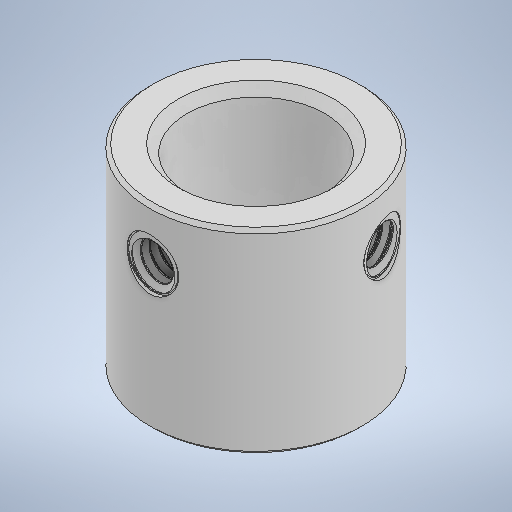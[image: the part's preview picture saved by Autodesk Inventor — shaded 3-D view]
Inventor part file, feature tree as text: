
AUTODESK INVENTOR PART (.ipt)
format: ipt  version: 2025.2 (Build 292293000, 293)  size: 747,520 bytes
history: native  units: mm
features: chamfer x2, extrude x1, plane x1, hole x1, thread x1, revolve x1, helix x1, pattern_circular x1, sketch x1
ambient origin geometry x8: Origin, YZ Plane, XZ Plane, XY Plane, X Axis, Y Axis, Z Axis, Center Point
bodies: Solid1 (feature_tree), Solid2 (feature_tree)
feature tree (10):
  extrude  "Extrusion1"  Depth=0.5005mm TaperAngle=45.0deg
  chamfer  "Chamfer1"  Distance=0.2mm Angle=45.0deg
  chamfer  "Chamfer2"  Distance=8.0mm
  plane  "Work Plane1"
  hole  "Hole1"  [1 undecoded]
  thread  "Thread1"  [1 undecoded]
  revolve  "Revolution1"  [1 undecoded]
  helix  "Coil1"  [1 undecoded]
  pattern_circular  "Circular Pattern1"  [2 undecoded]
  sketch  "Sketch4"  dims[d0=11.35mm d1=0.0mm d2=0.5mm d3=2.0mm d4=45.0deg d5=0.2mm d6=2.0mm d7=45.0deg d8=8.0mm d9=12.35mm d10=6.175mm d11=3.0mm d12=2.85mm d13=6.0mm d14=3.0mm d15=0.2mm d16=90.0deg d17=6.175mm d18=0.0mm d19=2.0mm d20=0.0mm d21=9.599311mm d22=0.080042mm d23=0.080042mm d26=0.5mm d28=9.599311mm d30=0.0mm d31=0.5005mm d32=3.0mm d33=10.0mm d34=0.0mm d35=0.0mm d36=0.0mm d37=0.0mm d38=0.0mm d39=20.0mm d40=105.0deg]
note: 6 required parameter values undecoded (feature->parameter linkage not recoverable at this tier; creation-order binding heuristic only, values carry confidence <= 0.55)